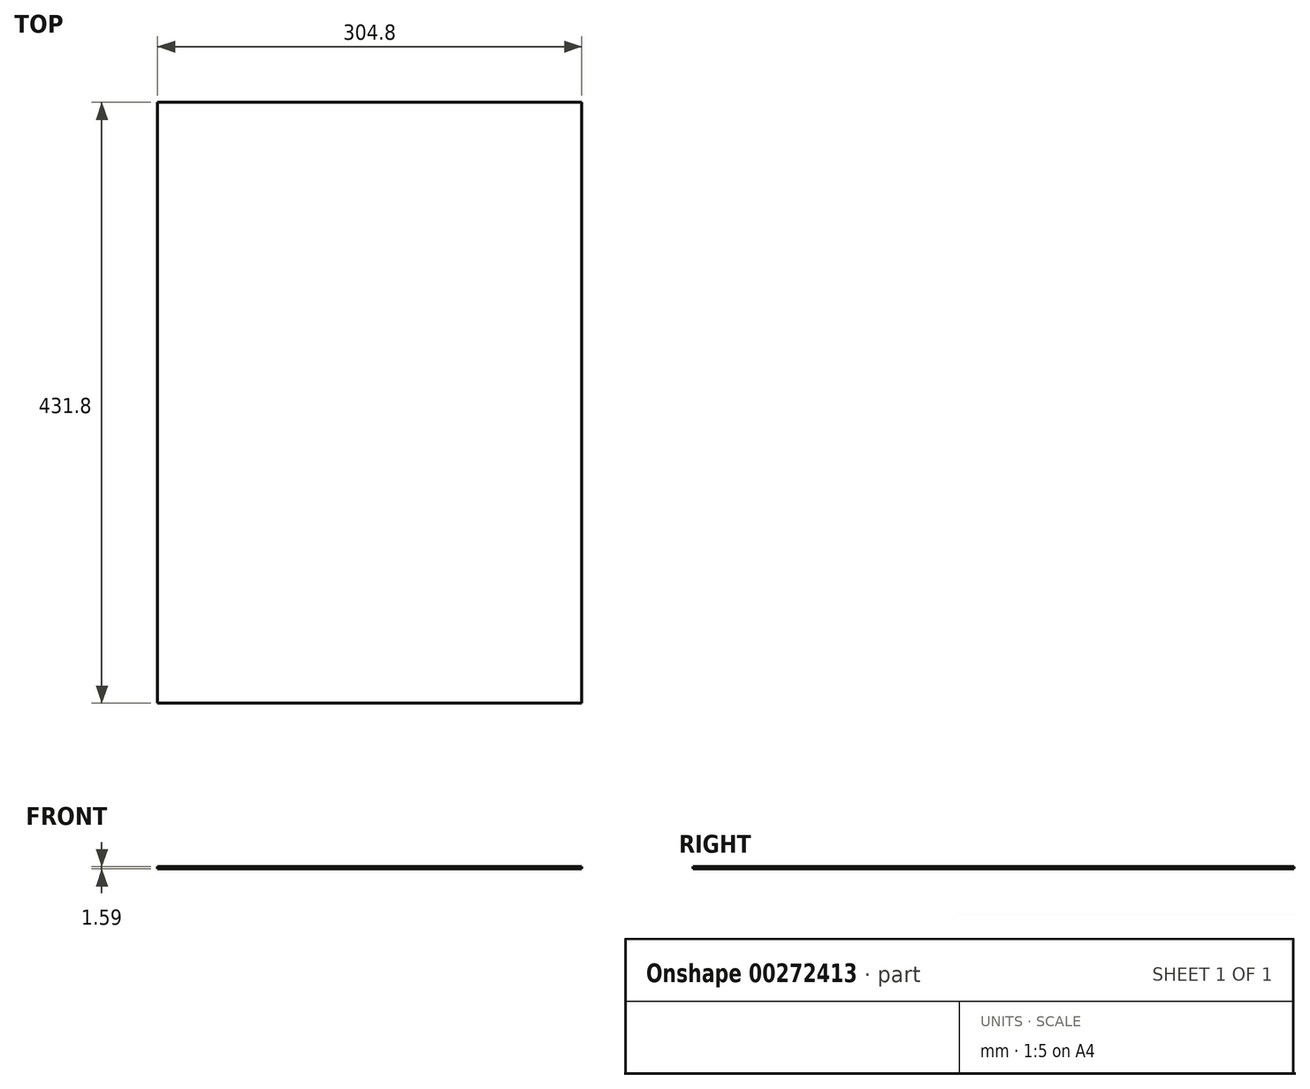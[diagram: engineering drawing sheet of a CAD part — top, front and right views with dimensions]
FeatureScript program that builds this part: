
annotation { "Feature Type Name" : "Feature", "Feature Type Description" : "" }
export const myFeature = defineFeature(function(context is Context, id is Id, definition is map)
    precondition{}
    {
        {
            var Q0;
            Q0=qCreatedBy(makeId("Top.planeOp"),FACE);
            var sketch = newSketch(context, id + "F0", { "sketchPlane" : qUnion([Q0])});
            skLineSegment(sketch, "E0.bottom", {"start": v(-152.4, 215.9) * mm, "end": v(152.4, 215.9) * mm});
            skLineSegment(sketch, "E0.top", {"start": v(-152.4, -215.9) * mm, "end": v(152.4, -215.9) * mm});
            skLineSegment(sketch, "E0.left", {"start": v(-152.4, 215.9) * mm, "end": v(-152.4, -215.9) * mm});
            skLineSegment(sketch, "E0.right", {"start": v(152.4, 215.9) * mm, "end": v(152.4, -215.9) * mm});
            skPoint(sketch, "E0.middle", {"position": v(0, 0) * mm});
            skSolve(sketch);
        }
        {
            var Q0;
            Q0=makeQuery(id+"F0.imprint","IMPRINT",FACE,{"disambiguationData":[TD([[makeQuery(id+"F0.imprint","IMPRINT",EDGE,{"derivedFrom":sQuery(id+"F0.wireOp",EDGE,"E0.bottom")}),-1.0]])]});
            var Q1;
            Q1 = qSketchRegion(id + "F0", true);
            extrude(context, id + "F1", {"entities" : qUnion([Q0, Q1]), "depth" : 1.59 * mm});
        }
    });
